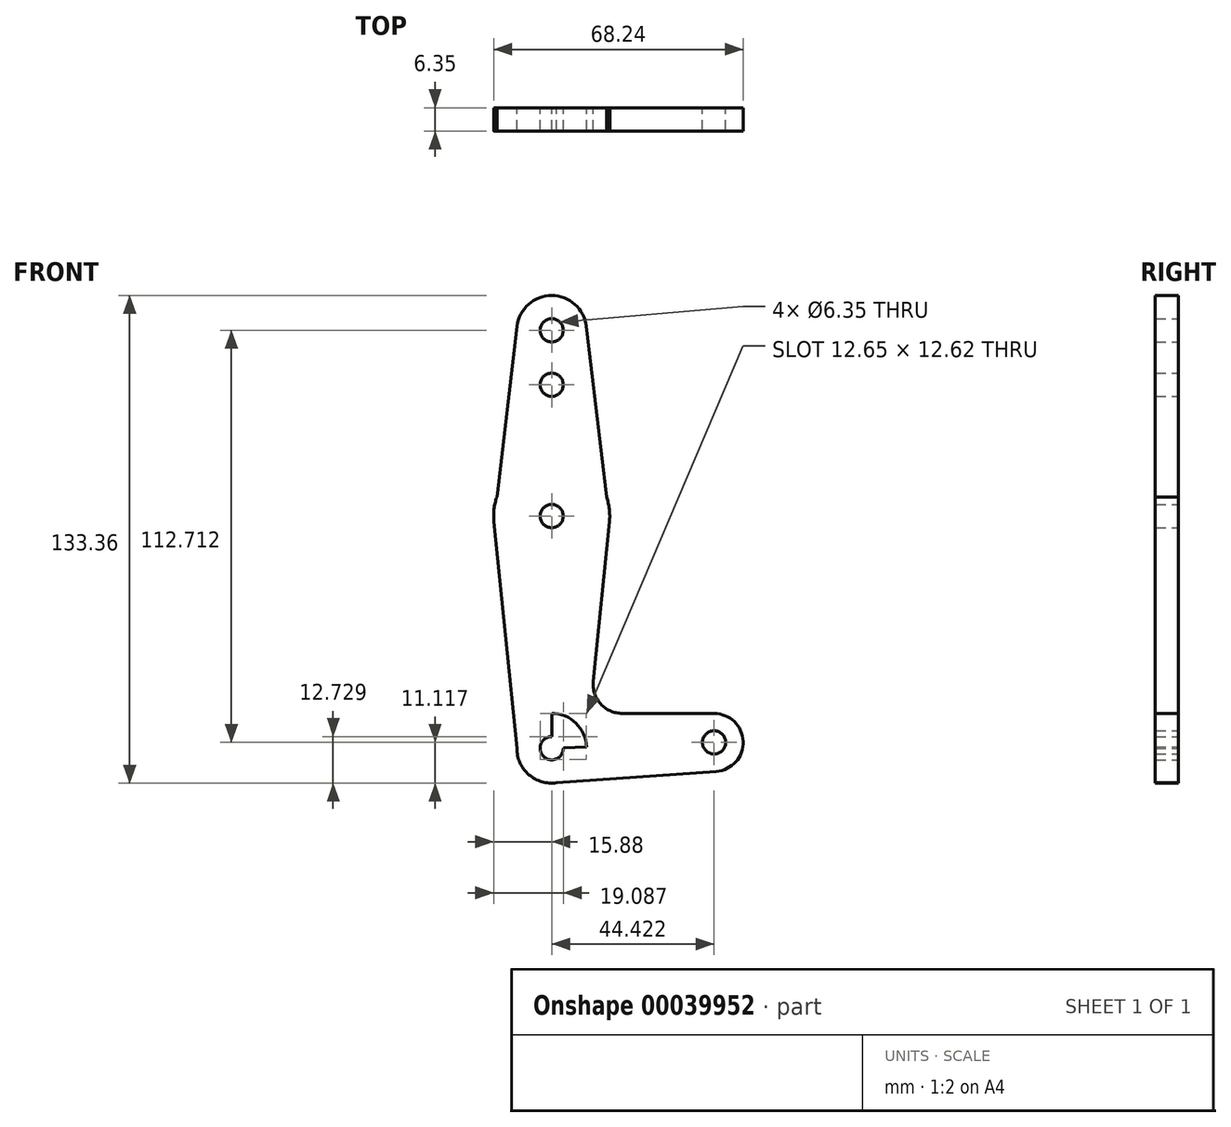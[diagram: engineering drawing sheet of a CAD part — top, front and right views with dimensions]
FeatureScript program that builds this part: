
annotation { "Feature Type Name" : "Feature", "Feature Type Description" : "" }
export const myFeature = defineFeature(function(context is Context, id is Id, definition is map)
    precondition{}
    {
        {
            var Q0;
            Q0=qCreatedBy(makeId("Front.planeOp"),FACE);
            var sketch = newSketch(context, id + "F0", { "sketchPlane" : qUnion([Q0])});
            skLineSegment(sketch, "E0", {"start": v(0, 114.3) * mm, "end": v(0, 0) * mm});
            skCircle(sketch, "E1", {"center": v(0, 114.3) * mm, "radius": 9.53 * mm});
            skCircle(sketch, "E2", {"center": v(0, 0) * mm, "radius": 9.53 * mm});
            skCircle(sketch, "E3", {"center": v(0, 63.5) * mm, "radius": 15.88 * mm});
            skCircle(sketch, "E4", {"center": v(44.42, 1.59) * mm, "radius": 7.94 * mm});
            skLineSegment(sketch, "E5", {"start": v(0, 0) * mm, "end": v(44.42, 1.59) * mm});
            skLineSegment(sketch, "E6", {"start": v(0, 63.5) * mm, "end": v(0, 0) * mm});
            skLineSegment(sketch, "E7", {"start": v(0, 0) * mm, "end": v(0, 63.5) * mm});
            skLineSegment(sketch, "E8", {"start": v(-15.8, 61.9) * mm, "end": v(-9.46, 115.42) * mm});
            skLineSegment(sketch, "E9", {"start": v(15.8, 61.9) * mm, "end": v(9.46, 115.42) * mm});
            skLineSegment(sketch, "E10", {"start": v(-9.52, 0) * mm, "end": v(-15.8, 61.9) * mm});
            skLineSegment(sketch, "E11", {"start": v(11.38, 18.28) * mm, "end": v(15.8, 61.9) * mm});
            skLineSegment(sketch, "E12", {"start": v(19.29, 9.53) * mm, "end": v(44.42, 9.53) * mm});
            skLineSegment(sketch, "E13", {"start": v(0, -9.53) * mm, "end": v(44.98, -6.33) * mm});
            skCircle(sketch, "E14", {"center": v(0, 114.3) * mm, "radius": 3.18 * mm});
            skCircle(sketch, "E15", {"center": v(0, 99.4) * mm, "radius": 3.18 * mm});
            skCircle(sketch, "E16", {"center": v(0, 63.5) * mm, "radius": 3.18 * mm});
            skCircle(sketch, "E17", {"center": v(0, 0) * mm, "radius": 3.18 * mm});
            skCircle(sketch, "E18", {"center": v(44.42, 1.59) * mm, "radius": 3.18 * mm});
            skPoint(sketch, "E19.newPointA", {"position": v(9.52, 0) * mm});
            skArc(sketch, "E19.filletArc", {"start": v(11.38, 18.28) * mm, "mid": v(13.39, 12.14) * mm, "end": v(19.29, 9.53) * mm});
            skSolve(sketch);
        }
        {
            var Q0;
            Q0 = qSketchRegion(id + "F0", true);
            var Q1;
            {var subQ3=sQuery(id+"F0.wireOp",EDGE,"E7");var subQ5=sQuery(id+"F0.wireOp",EDGE,"E2");var subQ7=makeQuery(id+"F0.imprint","INTERSECT",VERTEX,{"derivedFrom":[subQ5,subQ3]});Q1=makeQuery(id+"F0.imprint","IMPRINT",FACE,{"disambiguationData":[TD([[makeQuery(id+"F0.imprint","IMPRINT",EDGE,{"disambiguationData":[TD([[subQ7,1.0]])],"derivedFrom":subQ5}),1.0]])]});}
            extrude(context, id + "F1", {"entities" : qUnion([Q0, Q1]), "depth" : 6.35 * mm});
        }
    });
